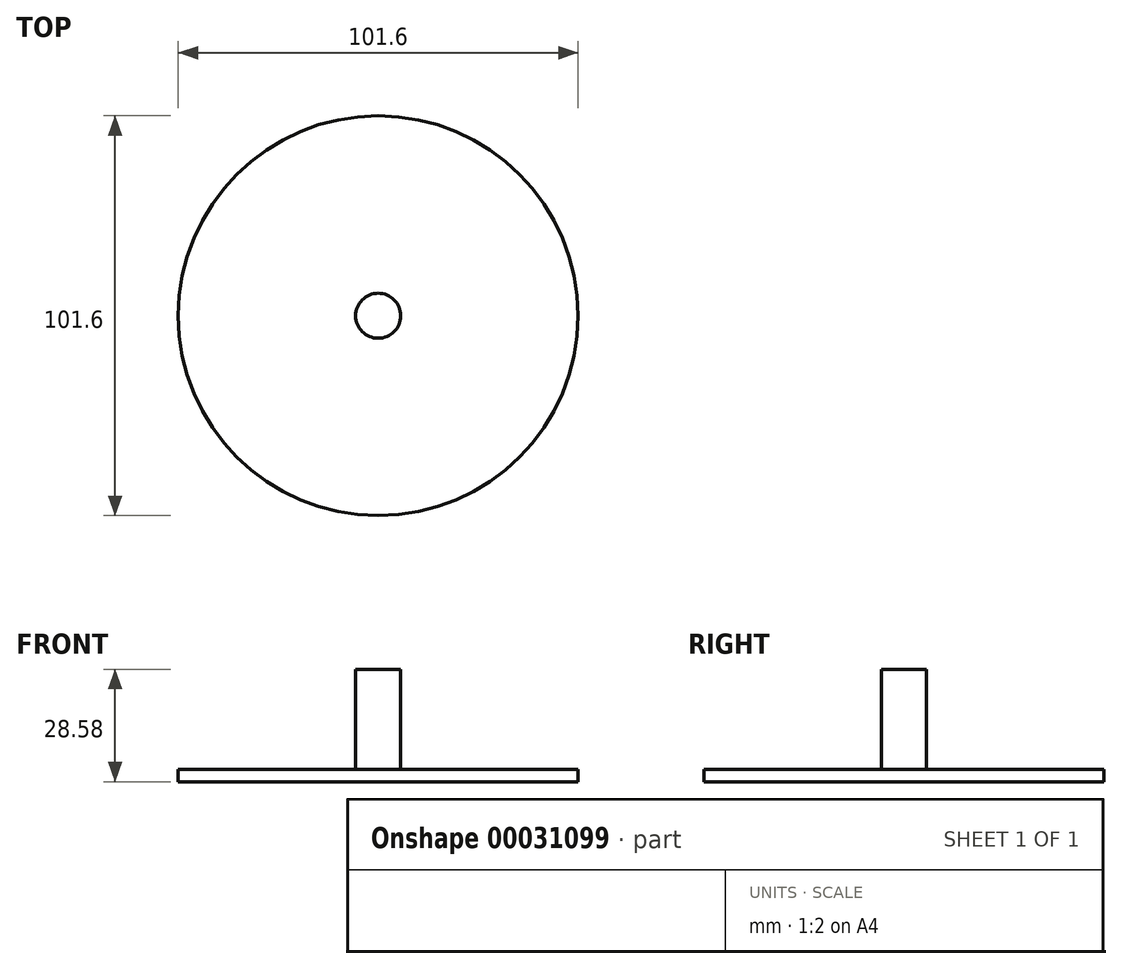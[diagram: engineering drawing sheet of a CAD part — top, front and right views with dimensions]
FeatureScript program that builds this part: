
annotation { "Feature Type Name" : "Feature", "Feature Type Description" : "" }
export const myFeature = defineFeature(function(context is Context, id is Id, definition is map)
    precondition{}
    {
        {
            var Q0;
            Q0=qCreatedBy(makeId("Top.planeOp"),FACE);
            var sketch = newSketch(context, id + "F0", { "sketchPlane" : qUnion([Q0])});
            skCircle(sketch, "E0", {"center": v(0, 0) * mm, "radius": 50.8 * mm});
            skSolve(sketch);
        }
        {
            var Q0;
            Q0=makeQuery(id+"F0.imprint","IMPRINT",FACE,{"disambiguationData":[TD([[makeQuery(id+"F0.imprint","IMPRINT",EDGE,{"derivedFrom":sQuery(id+"F0.wireOp",EDGE,"E0")}),1.0]])]});
            var Q1;
            Q1=sQuery(id+"F0.wireOp",EDGE,"E0");
            extrude(context, id + "F1", {"entities" : qUnion([Q0]), "surfaceEntities" : qUnion([Q1]), "depth" : 3.17 * mm});
        }
        {
            var Q0;
            Q0=makeQuery(id+"F1.opExtrude","CAP_FACE",FACE,{"disambiguationData":[OSD([sQuery(id+"F0.wireOp",EDGE,"E0")])],"isStart":false});
            var sketch = newSketch(context, id + "F2", { "sketchPlane" : qUnion([Q0])});
            skCircle(sketch, "E1", {"center": v(0, 0) * mm, "radius": 5.72 * mm});
            skSolve(sketch);
        }
        {
            var Q0;
            Q0=makeQuery(id+"F2.imprint","IMPRINT",FACE,{"disambiguationData":[TD([[makeQuery(id+"F2.imprint","IMPRINT",EDGE,{"derivedFrom":sQuery(id+"F2.wireOp",EDGE,"E1")}),1.0]])]});
            extrude(context, id + "F3", {"entities" : qUnion([Q0]), "operationType" : NewBodyOperationType.ADD, "depth" : 25.4 * mm});
        }
    });
